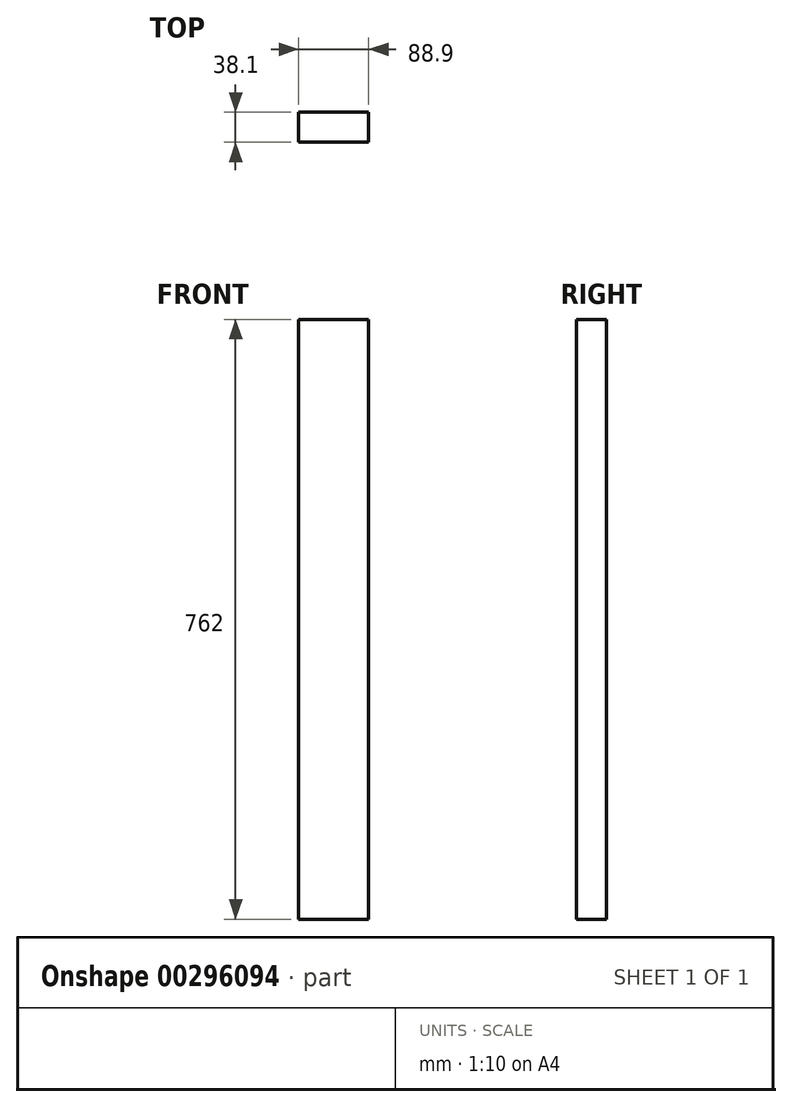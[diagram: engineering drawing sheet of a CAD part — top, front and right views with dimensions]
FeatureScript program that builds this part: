
annotation { "Feature Type Name" : "Feature", "Feature Type Description" : "" }
export const myFeature = defineFeature(function(context is Context, id is Id, definition is map)
    precondition{}
    {
        {
            var Q0;
            Q0=qCreatedBy(makeId("Front.planeOp"),FACE);
            var sketch = newSketch(context, id + "F0", { "sketchPlane" : qUnion([Q0])});
            skLineSegment(sketch, "E0.bottom", {"start": v(44.45, 381) * mm, "end": v(-44.45, 381) * mm});
            skLineSegment(sketch, "E0.top", {"start": v(44.45, -381) * mm, "end": v(-44.45, -381) * mm});
            skLineSegment(sketch, "E0.left", {"start": v(44.45, 381) * mm, "end": v(44.45, -381) * mm});
            skLineSegment(sketch, "E0.right", {"start": v(-44.45, 381) * mm, "end": v(-44.45, -381) * mm});
            skPoint(sketch, "E0.middle", {"position": v(0, 0) * mm});
            skSolve(sketch);
        }
        {
            var Q0;
            Q0=makeQuery(id+"F0.imprint","IMPRINT",FACE,{"disambiguationData":[TD([[makeQuery(id+"F0.imprint","IMPRINT",EDGE,{"derivedFrom":sQuery(id+"F0.wireOp",EDGE,"E0.bottom")}),1.0]])]});
            extrude(context, id + "F1", {"entities" : qUnion([Q0]), "depth" : 38.1 * mm});
        }
    });
